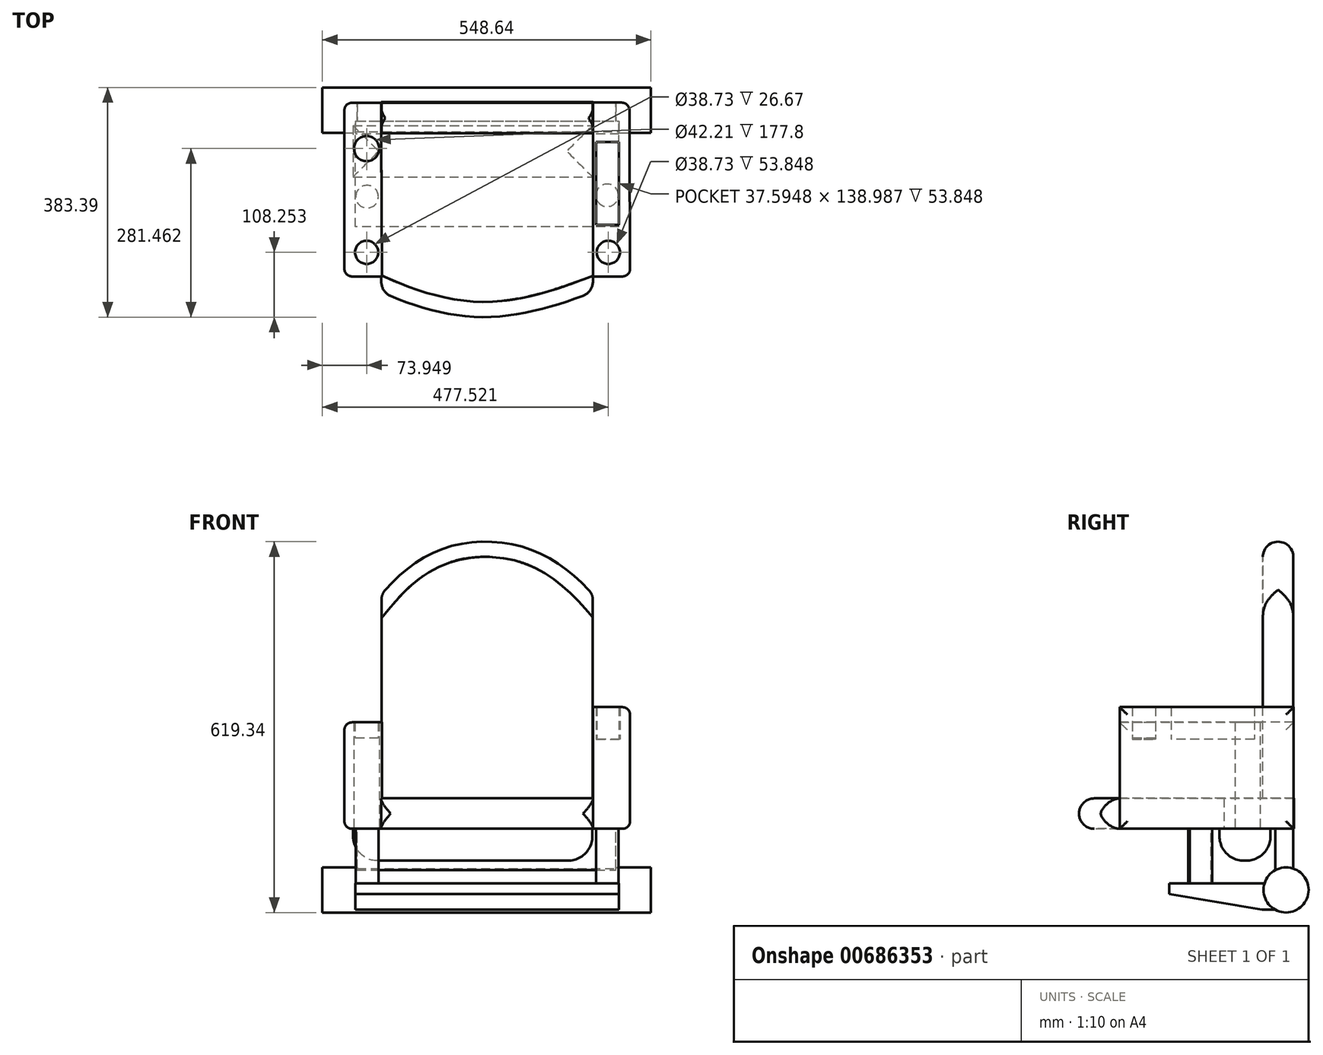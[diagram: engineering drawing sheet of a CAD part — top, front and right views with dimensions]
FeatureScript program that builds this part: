
annotation { "Feature Type Name" : "Feature", "Feature Type Description" : "" }
export const myFeature = defineFeature(function(context is Context, id is Id, definition is map)
    precondition{}
    {
        {
            var Q0;
            Q0=qCreatedBy(makeId("Top.planeOp"),FACE);
            var sketch = newSketch(context, id + "F0", { "sketchPlane" : qUnion([Q0])});
            skLineSegment(sketch, "E0", {"start": v(-96.99, -146.82) * mm, "end": v(-96.99, -315.82) * mm});
            skFitSpline(sketch, "E1", {"points": [v(-96.99, -315.82) * mm, v(71.33, -357.77) * mm, v(256.15, -315.82) * mm], "startDerivative": vector(281.84, -125.22) * mm, "endDerivative": vector(317.83, 122.35) * mm});
            skLineSegment(sketch, "E2", {"start": v(256.15, -315.82) * mm, "end": v(256.15, 1.38) * mm});
            skLineSegment(sketch, "E3", {"start": v(256.15, 1.38) * mm, "end": v(-96.99, 1.38) * mm});
            skLineSegment(sketch, "E4", {"start": v(-96.99, 1.38) * mm, "end": v(-96.99, -146.82) * mm});
            skSolve(sketch);
        }
        {
            var Q0;
            Q0=makeQuery(id+"F0.imprint","IMPRINT",FACE,{"disambiguationData":[TD([[makeQuery(id+"F0.imprint","IMPRINT",EDGE,{"derivedFrom":sQuery(id+"F0.wireOp",EDGE,"E0")}),1.0]])]});
            extrude(context, id + "F1", {"entities" : qUnion([Q0]), "depth" : 50.8 * mm, "offsetDistance" : 25.4 * mm});
        }
        {
            var Q0;
            Q0=qCreatedBy(makeId("Front.planeOp"),FACE);
            var sketch = newSketch(context, id + "F2", { "sketchPlane" : qUnion([Q0])});
            skLineSegment(sketch, "E5", {"start": v(-96.8, 0) * mm, "end": v(-96.8, 391.55) * mm});
            skLineSegment(sketch, "E6", {"start": v(256.07, 0) * mm, "end": v(256.07, 391.55) * mm});
            skLineSegment(sketch, "E7", {"start": v(-96.8, 0) * mm, "end": v(256.07, 0) * mm});
            skFitSpline(sketch, "E8", {"points": [v(-96.8, 391.55) * mm, v(74.83, 479.55) * mm, v(256.07, 391.55) * mm], "startDerivative": vector(340.56, 406.57) * mm, "endDerivative": vector(365.1, -403.69) * mm});
            skSolve(sketch);
        }
        {
            var Q0;
            Q0=makeQuery(id+"F2.imprint","IMPRINT",FACE,{"disambiguationData":[TD([[makeQuery(id+"F2.imprint","IMPRINT",EDGE,{"derivedFrom":sQuery(id+"F2.wireOp",EDGE,"E5")}),-1.0]])]});
            extrude(context, id + "F3", {"entities" : qUnion([Q0]), "operationType" : NewBodyOperationType.ADD, "depth" : 50.8 * mm, "offsetDistance" : 25.4 * mm});
        }
        {
            var Q0;
            Q0=makeQuery(id+"F1.opExtrude","SWEPT_FACE",FACE,{"disambiguationData":[OSD([sQuery(id+"F0.wireOp",EDGE,"E1")])]});
            fillet(context, id + "F4", {"entities" : qUnion([Q0]), "radius" : 25.4 * mm, "tangentPropagation" : true, "allowEdgeOverflow" : false});
        }
        {
            var Q0;
            Q0=makeQuery(id+"F3.opExtrude","SWEPT_FACE",FACE,{"disambiguationData":[OSD([sQuery(id+"F2.wireOp",EDGE,"E8")])]});
            fillet(context, id + "F5", {"entities" : qUnion([Q0]), "radius" : 25.4 * mm, "tangentPropagation" : true, "allowEdgeOverflow" : false});
        }
        {
            var Q0;
            Q0=qCreatedBy(makeId("Top.planeOp"),FACE);
            var sketch = newSketch(context, id + "F6", { "sketchPlane" : qUnion([Q0])});
            skLineSegment(sketch, "E9", {"start": v(-97.3, -52.82) * mm, "end": v(-158.8, -52.82) * mm});
            skLineSegment(sketch, "E10", {"start": v(-158.8, -289.78) * mm, "end": v(-96.15, -289.78) * mm});
            skLineSegment(sketch, "E11", {"start": v(-96.15, -289.78) * mm, "end": v(-97.3, -52.82) * mm});
            skLineSegment(sketch, "E12", {"start": v(-158.8, -52.82) * mm, "end": v(-158.8, -289.78) * mm});
            skCircle(sketch, "E13", {"center": v(-121.63, -249.53) * mm, "radius": 19.37 * mm});
            skLineSegment(sketch, "E14", {"start": v(317.2, -52.82) * mm, "end": v(255.69, -52.82) * mm});
            skLineSegment(sketch, "E15", {"start": v(255.69, -289.78) * mm, "end": v(318.34, -289.78) * mm});
            skLineSegment(sketch, "E16", {"start": v(318.34, -289.78) * mm, "end": v(317.2, -52.82) * mm});
            skLineSegment(sketch, "E17", {"start": v(255.69, -52.82) * mm, "end": v(255.69, -289.78) * mm});
            skCircle(sketch, "E18", {"center": v(281.94, -249.53) * mm, "radius": 19.37 * mm});
            skLineSegment(sketch, "E19.bottom", {"start": v(261.76, -64.97) * mm, "end": v(299.36, -64.97) * mm});
            skLineSegment(sketch, "E19.top", {"start": v(261.76, -203.96) * mm, "end": v(299.36, -203.96) * mm});
            skLineSegment(sketch, "E19.left", {"start": v(261.76, -64.97) * mm, "end": v(261.76, -203.96) * mm});
            skLineSegment(sketch, "E19.right", {"start": v(299.36, -64.97) * mm, "end": v(299.36, -203.96) * mm});
            skCircle(sketch, "E20", {"center": v(-121.63, -76.32) * mm, "radius": 21.1 * mm});
            skSolve(sketch);
        }
        {
            var Q0;
            Q0=makeQuery(id+"F6.imprint","IMPRINT",FACE,{"disambiguationData":[TD([[makeQuery(id+"F6.imprint","IMPRINT",EDGE,{"derivedFrom":sQuery(id+"F6.wireOp",EDGE,"E9")}),1.0]])]});
            extrude(context, id + "F7", {"entities" : qUnion([Q0]), "operationType" : NewBodyOperationType.ADD, "depth" : 177.8 * mm, "offsetDistance" : 25.4 * mm});
        }
        {
            var Q0;
            Q0=makeQuery(id+"F7.opExtrude","SWEPT_FACE",FACE,{"disambiguationData":[OSD([sQuery(id+"F6.wireOp",EDGE,"E9")])]});
            extrude(context, id + "F8", {"entities" : qUnion([Q0]), "operationType" : NewBodyOperationType.ADD, "depth" : 53.1 * mm, "offsetDistance" : 25.4 * mm});
        }
        {
            var Q0;
            Q0 = qSketchRegion(id + "F6", true);
            extrude(context, id + "F9", {"entities" : qUnion([Q0]), "operationType" : NewBodyOperationType.ADD, "depth" : 25.4 * mm, "offsetDistance" : 25.4 * mm});
        }
        {
            var Q0;
            Q0=makeQuery(id+"F9.opExtrude","CAP_FACE",FACE,{"disambiguationData":[OSD([sQuery(id+"F6.wireOp",EDGE,"E14"),sQuery(id+"F6.wireOp",EDGE,"E15"),sQuery(id+"F6.wireOp",EDGE,"E16"),sQuery(id+"F6.wireOp",EDGE,"E17"),sQuery(id+"F6.wireOp",EDGE,"E18")])],"isStart":false});
            extrude(context, id + "F10", {"entities" : qUnion([Q0]), "operationType" : NewBodyOperationType.ADD, "depth" : 177.8 * mm, "offsetDistance" : 25.4 * mm});
        }
        {
            var Q0;
            {var subQ0=sQuery(id+"F6.wireOp",EDGE,"E14");Q0=makeQuery(id+"F10.boolean.opBoolean","MERGE",FACE,{"derivedFrom":[makeQuery(id+"F9.opExtrude","SWEPT_FACE",FACE,{"disambiguationData":[OSD([subQ0])]}),makeQuery(id+"F10.opExtrude","SWEPT_FACE",FACE,{"disambiguationData":[OSD([subQ0])]})]});}
            extrude(context, id + "F11", {"entities" : qUnion([Q0]), "operationType" : NewBodyOperationType.ADD, "depth" : 53.34 * mm, "offsetDistance" : 25.4 * mm});
        }
        {
            var Q0;
            {var subQ0=sQuery(id+"F6.wireOp",EDGE,"E16");Q0=makeQuery(id+"F10.boolean.opBoolean","MERGE",FACE,{"derivedFrom":[makeQuery(id+"F9.opExtrude","SWEPT_FACE",FACE,{"disambiguationData":[OSD([subQ0])]}),makeQuery(id+"F10.opExtrude","SWEPT_FACE",FACE,{"disambiguationData":[OSD([subQ0])]})]});}
            var Q1;
            Q1=makeQuery(id+"F11.opExtrude","SWEPT_FACE",FACE,{"disambiguationData":[OSD([sQuery(id+"F6.wireOp",EDGE,"E14"),sQuery(id+"F6.wireOp",EDGE,"E16")])]});
            fillet(context, id + "F12", {"entities" : qUnion([Q0, Q1]), "radius" : 12.7 * mm, "tangentPropagation" : true, "allowEdgeOverflow" : false});
        }
        {
            var Q0;
            {var subQ0=sQuery(id+"F6.wireOp",EDGE,"E12");Q0=makeQuery(id+"F8.boolean.opBoolean","MERGE",FACE,{"derivedFrom":[makeQuery(id+"F7.opExtrude","SWEPT_FACE",FACE,{"disambiguationData":[OSD([subQ0])]}),makeQuery(id+"F8.opExtrude","SWEPT_FACE",FACE,{"disambiguationData":[OSD([sQuery(id+"F6.wireOp",EDGE,"E9"),subQ0])]})]});}
            fillet(context, id + "F13", {"entities" : qUnion([Q0]), "radius" : 12.7 * mm, "tangentPropagation" : true, "allowEdgeOverflow" : false});
        }
        {
            var Q0;
            Q0=qCreatedBy(makeId("Top.planeOp"),FACE);
            var sketch = newSketch(context, id + "F14", { "sketchPlane" : qUnion([Q0])});
            skLineSegment(sketch, "E21.bottom", {"start": v(-144.18, -37.98) * mm, "end": v(255.37, -37.98) * mm});
            skLineSegment(sketch, "E21.top", {"start": v(-144.18, -123.37) * mm, "end": v(255.37, -123.37) * mm});
            skLineSegment(sketch, "E21.left", {"start": v(-144.18, -37.98) * mm, "end": v(-144.18, -123.37) * mm});
            skLineSegment(sketch, "E21.right", {"start": v(255.37, -37.98) * mm, "end": v(255.37, -123.37) * mm});
            skSolve(sketch);
        }
        {
            var Q0;
            Q0=makeQuery(id+"F14.imprint","IMPRINT",FACE,{"disambiguationData":[TD([[makeQuery(id+"F14.imprint","IMPRINT",EDGE,{"derivedFrom":sQuery(id+"F14.wireOp",EDGE,"E21.bottom")}),-1.0]])]});
            extrude(context, id + "F15", {"entities" : qUnion([Q0]), "operationType" : NewBodyOperationType.ADD, "oppositeDirection" : true, "depth" : 53.34 * mm, "offsetDistance" : 25.4 * mm});
        }
        {
            var Q0;
            Q0=makeQuery(id+"F15.opExtrude","CAP_FACE",FACE,{"disambiguationData":[OSD([sQuery(id+"F14.wireOp",EDGE,"E21.bottom"),sQuery(id+"F14.wireOp",EDGE,"E21.top"),sQuery(id+"F14.wireOp",EDGE,"E21.left"),sQuery(id+"F14.wireOp",EDGE,"E21.right")])],"isStart":false});
            fillet(context, id + "F16", {"entities" : qUnion([Q0]), "radius" : 41.1 * mm, "tangentPropagation" : true, "allowEdgeOverflow" : false});
        }
        {
            var Q0;
            Q0=qCreatedBy(makeId("Top.planeOp"),FACE);
            var sketch = newSketch(context, id + "F17", { "sketchPlane" : qUnion([Q0])});
            skLineSegment(sketch, "E22.bottom", {"start": v(259.45, -59.27) * mm, "end": v(302.17, -59.27) * mm});
            skLineSegment(sketch, "E22.top", {"start": v(259.45, -277.44) * mm, "end": v(302.17, -277.44) * mm});
            skLineSegment(sketch, "E22.left", {"start": v(259.45, -59.27) * mm, "end": v(259.45, -277.44) * mm});
            skLineSegment(sketch, "E22.right", {"start": v(302.17, -59.27) * mm, "end": v(302.17, -277.44) * mm});
            skLineSegment(sketch, "E23.bottom", {"start": v(-142.13, -223.9) * mm, "end": v(-101.12, -223.9) * mm});
            skLineSegment(sketch, "E23.top", {"start": v(-142.13, -277.44) * mm, "end": v(-101.12, -277.44) * mm});
            skLineSegment(sketch, "E23.left", {"start": v(-142.13, -223.9) * mm, "end": v(-142.13, -277.44) * mm});
            skLineSegment(sketch, "E23.right", {"start": v(-101.12, -223.9) * mm, "end": v(-101.12, -277.44) * mm});
            skSolve(sketch);
        }
        {
            var Q0;
            Q0=makeQuery(id+"F17.imprint","IMPRINT",FACE,{"disambiguationData":[TD([[makeQuery(id+"F17.imprint","IMPRINT",EDGE,{"derivedFrom":sQuery(id+"F17.wireOp",EDGE,"E22.bottom")}),-1.0]])]});
            extrude(context, id + "F18", {"entities" : qUnion([Q0]), "operationType" : NewBodyOperationType.ADD, "depth" : 149.35 * mm, "offsetDistance" : 25.4 * mm});
        }
        {
            var Q0;
            Q0=makeQuery(id+"F17.imprint","IMPRINT",FACE,{"disambiguationData":[TD([[makeQuery(id+"F17.imprint","IMPRINT",EDGE,{"derivedFrom":sQuery(id+"F17.wireOp",EDGE,"E23.bottom")}),-1.0]])]});
            extrude(context, id + "F19", {"entities" : qUnion([Q0]), "operationType" : NewBodyOperationType.ADD, "depth" : 151.13 * mm, "offsetDistance" : 25.4 * mm});
        }
        {
            var Q0;
            Q0=qCreatedBy(makeId("Top.planeOp"),FACE);
            var sketch = newSketch(context, id + "F20", { "sketchPlane" : qUnion([Q0])});
            skLineSegment(sketch, "E24.bottom", {"start": v(-137.52, 0) * mm, "end": v(294.53, 0) * mm});
            skLineSegment(sketch, "E24.top", {"start": v(-137.52, -30.1) * mm, "end": v(294.53, -30.1) * mm});
            skLineSegment(sketch, "E24.left", {"start": v(-137.52, 0) * mm, "end": v(-137.52, -30.1) * mm});
            skLineSegment(sketch, "E24.right", {"start": v(294.53, 0) * mm, "end": v(294.53, -30.1) * mm});
            skSolve(sketch);
        }
        {
            var Q0;
            Q0 = qSketchRegion(id + "F20", true);
            extrude(context, id + "F21", {"entities" : qUnion([Q0]), "operationType" : NewBodyOperationType.ADD, "oppositeDirection" : true, "depth" : 124.46 * mm, "offsetDistance" : 25.4 * mm});
        }
        {
            var Q0;
            Q0=makeQuery(id+"F21.opExtrude","CAP_FACE",FACE,{"disambiguationData":[OSD([sQuery(id+"F20.wireOp",EDGE,"E24.bottom"),sQuery(id+"F20.wireOp",EDGE,"E24.top"),sQuery(id+"F20.wireOp",EDGE,"E24.left"),sQuery(id+"F20.wireOp",EDGE,"E24.right")])],"isStart":false});
            fillet(context, id + "F22", {"entities" : qUnion([Q0]), "radius" : 12.26 * mm, "tangentPropagation" : true, "allowEdgeOverflow" : false});
        }
        {
            var Q0;
            Q0=qCreatedBy(makeId("Right.planeOp"),FACE);
            var sketch = newSketch(context, id + "F23", { "sketchPlane" : qUnion([Q0])});
            skCircle(sketch, "E25", {"center": v(-12.06, -102.11) * mm, "radius": 37.67 * mm});
            skSolve(sketch);
        }
        {
            var Q0;
            Q0=makeQuery(id+"F23.imprint","IMPRINT",FACE,{"disambiguationData":[TD([[makeQuery(id+"F23.imprint","IMPRINT",EDGE,{"derivedFrom":sQuery(id+"F23.wireOp",EDGE,"E25")}),1.0]])]});
            extrude(context, id + "F24", {"entities" : qUnion([Q0]), "operationType" : NewBodyOperationType.ADD, "oppositeDirection" : true, "depth" : 139.7 * mm, "offsetDistance" : 25.4 * mm});
        }
        {
            var Q0;
            Q0=makeQuery(id+"F24.opExtrude","CAP_FACE",FACE,{"disambiguationData":[OSD([sQuery(id+"F23.wireOp",EDGE,"E25")])],"isStart":false});
            extrude(context, id + "F25", {"entities" : qUnion([Q0]), "operationType" : NewBodyOperationType.ADD, "depth" : 25.4 * mm, "offsetDistance" : 25.4 * mm, "hasSecondDirection" : true, "secondDirectionOppositeDirection" : true, "secondDirectionDepth" : 438.15 * mm});
        }
        {
            var Q0;
            Q0=makeQuery(id+"F25.opExtrude","CAP_FACE",FACE,{"disambiguationData":[OSD([sQuery(id+"F23.wireOp",EDGE,"E25")])],"isStart":false});
            extrude(context, id + "F26", {"entities" : qUnion([Q0]), "operationType" : NewBodyOperationType.ADD, "oppositeDirection" : true, "depth" : 22.86 * mm, "offsetDistance" : 25.4 * mm, "hasSecondDirection" : true, "secondDirectionOppositeDirection" : false, "secondDirectionDepth" : 25.4 * mm});
        }
        {
            var Q0;
            Q0=makeQuery(id+"F26.opExtrude","CAP_FACE",FACE,{"disambiguationData":[OSD([sQuery(id+"F23.wireOp",EDGE,"E25")])],"isStart":true});
            extrude(context, id + "F27", {"entities" : qUnion([Q0]), "operationType" : NewBodyOperationType.ADD, "depth" : 5.08 * mm, "offsetDistance" : 25.4 * mm, "hasSecondDirection" : true, "secondDirectionOppositeDirection" : true, "secondDirectionDepth" : 543.56 * mm});
        }
        {
            var Q0;
            Q0=qCreatedBy(makeId("Top.planeOp"),FACE);
            var sketch = newSketch(context, id + "F28", { "sketchPlane" : qUnion([Q0])});
            skCircle(sketch, "E26", {"center": v(-120.91, -156.58) * mm, "radius": 18.94 * mm});
            skCircle(sketch, "E27", {"center": v(280.1, -154.3) * mm, "radius": 18.87 * mm});
            skSolve(sketch);
        }
        {
            var Q0;
            Q0=makeQuery(id+"F28.imprint","IMPRINT",FACE,{"disambiguationData":[TD([[makeQuery(id+"F28.imprint","IMPRINT",EDGE,{"derivedFrom":sQuery(id+"F28.wireOp",EDGE,"E27")}),1.0]])]});
            extrude(context, id + "F29", {"entities" : qUnion([Q0]), "operationType" : NewBodyOperationType.ADD, "oppositeDirection" : true, "depth" : 100.84 * mm, "offsetDistance" : 25.4 * mm});
        }
        {
            var Q0;
            Q0=makeQuery(id+"F28.imprint","IMPRINT",FACE,{"disambiguationData":[TD([[makeQuery(id+"F28.imprint","IMPRINT",EDGE,{"derivedFrom":sQuery(id+"F28.wireOp",EDGE,"E26")}),1.0]])]});
            extrude(context, id + "F30", {"entities" : qUnion([Q0]), "operationType" : NewBodyOperationType.ADD, "oppositeDirection" : true, "depth" : 100.84 * mm, "offsetDistance" : 25.4 * mm});
        }
        {
            var Q0;
            Q0=qCreatedBy(makeId("Right.planeOp"),FACE);
            var sketch = newSketch(context, id + "F31", { "sketchPlane" : qUnion([Q0])});
            skLineSegment(sketch, "E28", {"start": v(-206.95, -91.27) * mm, "end": v(-168.19, -91.27) * mm});
            skLineSegment(sketch, "E29", {"start": v(-206.95, -91.27) * mm, "end": v(-206.95, -108.88) * mm});
            skLineSegment(sketch, "E30", {"start": v(-206.95, -108.88) * mm, "end": v(-52.03, -134.9) * mm});
            skLineSegment(sketch, "E31", {"start": v(-52.03, -134.9) * mm, "end": v(-52.03, -91.27) * mm});
            skLineSegment(sketch, "E32", {"start": v(-52.03, -91.27) * mm, "end": v(-168.19, -91.27) * mm});
            skSolve(sketch);
        }
        {
            var Q0;
            Q0=makeQuery(id+"F31.imprint","IMPRINT",FACE,{"disambiguationData":[TD([[makeQuery(id+"F31.imprint","IMPRINT",EDGE,{"derivedFrom":sQuery(id+"F31.wireOp",EDGE,"E28")}),-1.0]])]});
            extrude(context, id + "F32", {"entities" : qUnion([Q0]), "operationType" : NewBodyOperationType.ADD, "depth" : 299.72 * mm, "offsetDistance" : 25.4 * mm, "hasSecondDirection" : true, "secondDirectionOppositeDirection" : true, "secondDirectionDepth" : 140.72 * mm});
        }
        {
            var Q0;
            Q0=makeQuery(id+"F32.opExtrude","SWEPT_FACE",FACE,{"disambiguationData":[OSD([sQuery(id+"F31.wireOp",EDGE,"E31")])]});
            extrude(context, id + "F33", {"entities" : qUnion([Q0]), "operationType" : NewBodyOperationType.ADD, "depth" : 25.4 * mm, "offsetDistance" : 25.4 * mm});
        }
    });
